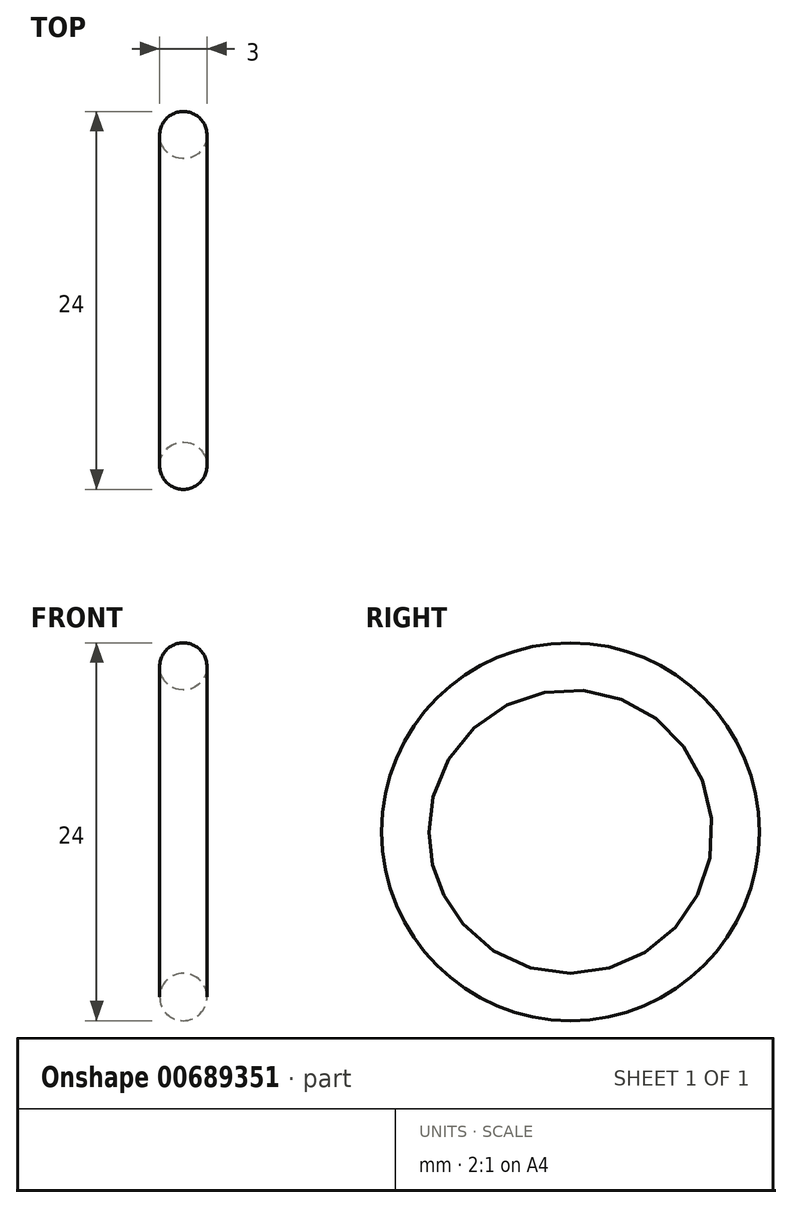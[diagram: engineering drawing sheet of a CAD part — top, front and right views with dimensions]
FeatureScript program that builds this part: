
annotation { "Feature Type Name" : "Feature", "Feature Type Description" : "" }
export const myFeature = defineFeature(function(context is Context, id is Id, definition is map)
    precondition{}
    {
        {
            var Q0;
            Q0=qCreatedBy(makeId("Front.planeOp"),FACE);
            var sketch = newSketch(context, id + "F0", { "sketchPlane" : qUnion([Q0])});
            skCircle(sketch, "E0", {"center": v(0, 10.5) * mm, "radius": 1.5 * mm});
            skSolve(sketch);
        }
        {
            var Q0;
            Q0=qCreatedBy(makeId("Top.planeOp"),FACE);
            var sketch = newSketch(context, id + "F1", { "sketchPlane" : qUnion([Q0])});
            skLineSegment(sketch, "E1", {"start": v(61.08, 0) * mm, "end": v(-58.9, 0) * mm});
            skSolve(sketch);
        }
        {
            var Q0;
            Q0=qSketchRegion(id+"F0",true);
            var Q1;
            Q1=sQuery(id+"F1.wireOp",EDGE,"E1");
            revolve(context, id + "F2", {"entities" : qUnion([Q0]), "axis" : qUnion([Q1]), "revolveType" : RevolveType.FULL});
        }
    });
